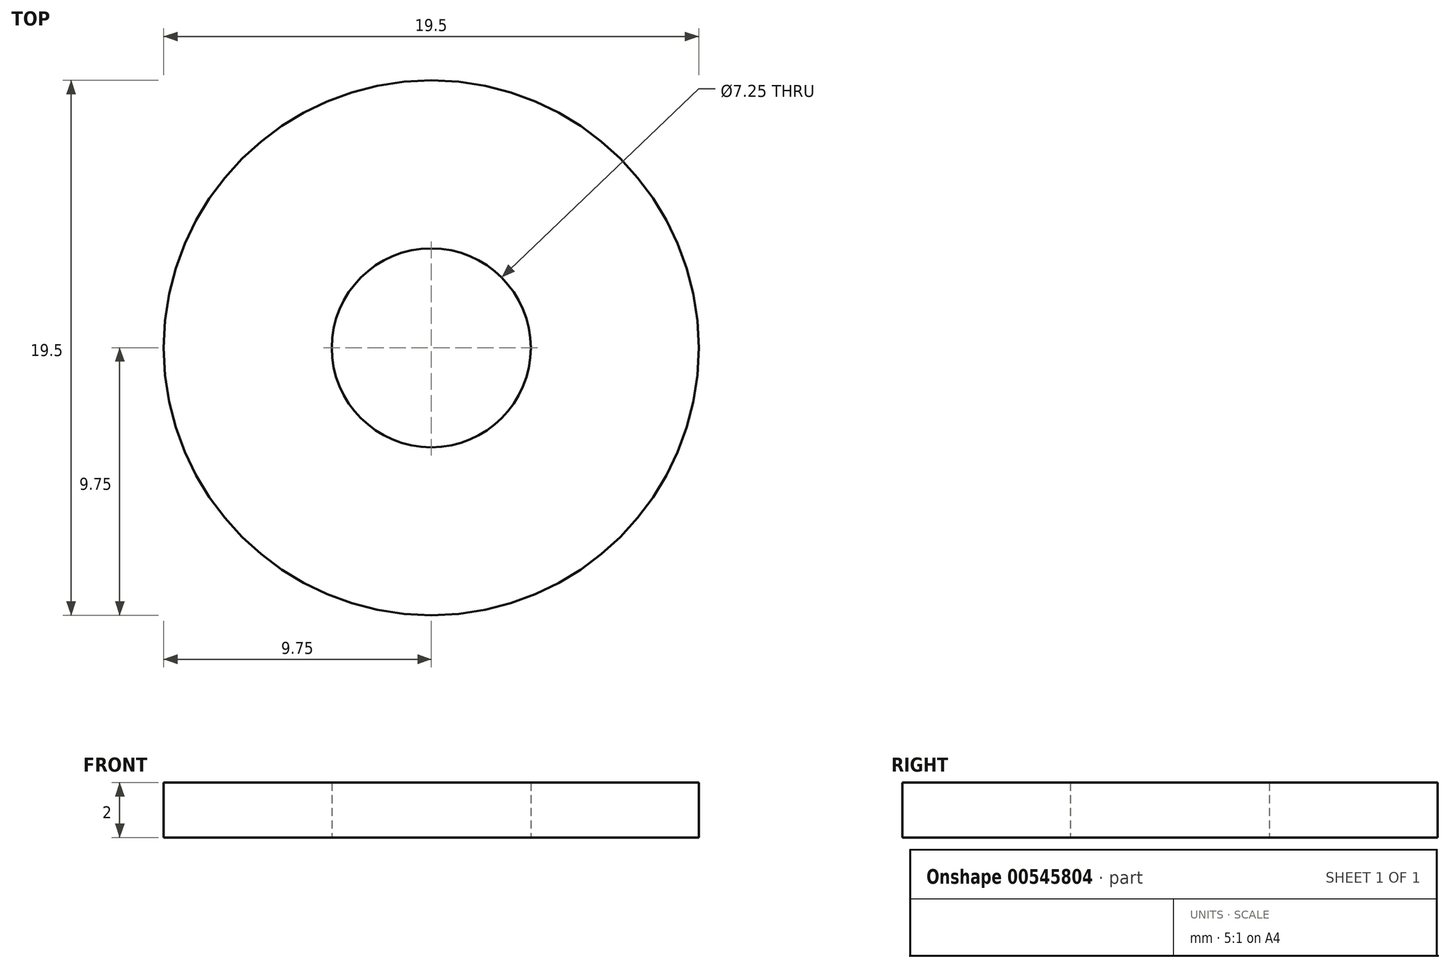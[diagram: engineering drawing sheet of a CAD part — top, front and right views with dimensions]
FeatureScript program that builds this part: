
annotation { "Feature Type Name" : "Feature", "Feature Type Description" : "" }
export const myFeature = defineFeature(function(context is Context, id is Id, definition is map)
    precondition{}
    {
        {
            var Q0;
            Q0=qCreatedBy(makeId("Top.planeOp"),FACE);
            var sketch = newSketch(context, id + "F0", { "sketchPlane" : qUnion([Q0])});
            skCircle(sketch, "E0", {"center": v(0, 0) * mm, "radius": 9.75 * mm});
            skCircle(sketch, "E1", {"center": v(0, 0) * mm, "radius": 3.62 * mm});
            skSolve(sketch);
        }
        {
            var Q0;
            Q0 = qSketchRegion(id + "F0", true);
            extrude(context, id + "F1", {"entities" : qUnion([Q0]), "depth" : 2 * mm, "offsetDistance" : 25 * mm});
        }
    });
